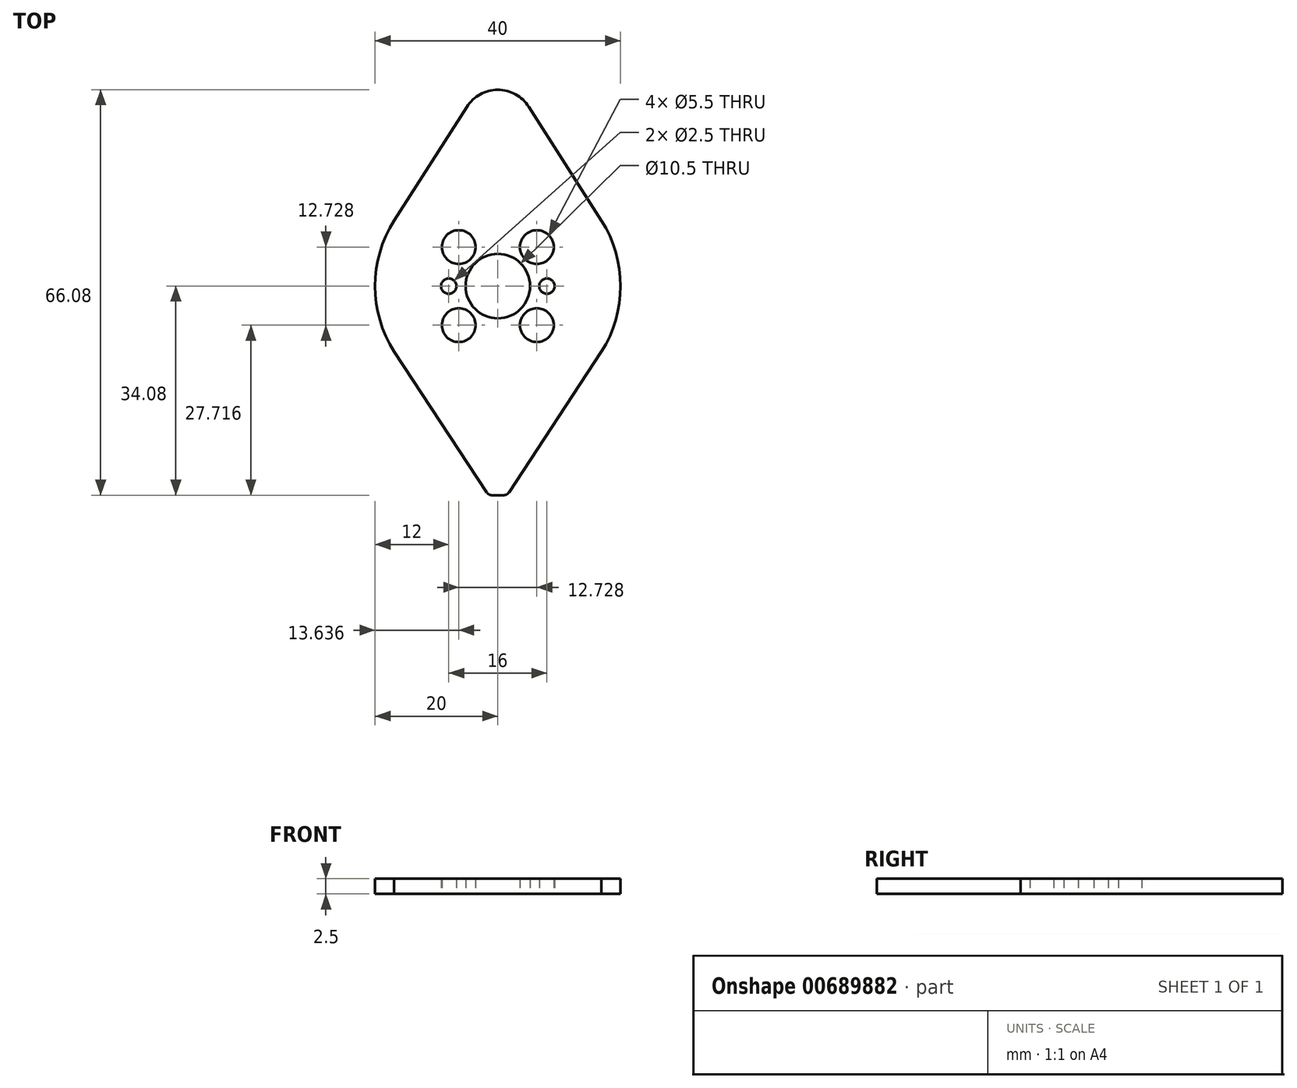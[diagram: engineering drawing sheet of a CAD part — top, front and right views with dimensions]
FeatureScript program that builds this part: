
annotation { "Feature Type Name" : "Feature", "Feature Type Description" : "" }
export const myFeature = defineFeature(function(context is Context, id is Id, definition is map)
    precondition{}
    {
        {
            var Q0;
            Q0=qCreatedBy(makeId("Top.planeOp"),FACE);
            var sketch = newSketch(context, id + "F0", { "sketchPlane" : qUnion([Q0])});
            skCircle(sketch, "E0", {"center": v(0, 0) * mm, "radius": 20 * mm});
            skCircle(sketch, "E1", {"center": v(0, 26) * mm, "radius": 6 * mm});
            skLineSegment(sketch, "E2", {"start": v(16.9, 10.7) * mm, "end": v(5.06, 29.23) * mm});
            skLineSegment(sketch, "E3", {"start": v(-5.06, 29.23) * mm, "end": v(-16.9, 10.7) * mm});
            skLineSegment(sketch, "E4", {"start": v(-16.9, -10.7) * mm, "end": v(-1.8, -33.63) * mm});
            skLineSegment(sketch, "E5", {"start": v(-0.96, -34.08) * mm, "end": v(0.96, -34.08) * mm});
            skLineSegment(sketch, "E6", {"start": v(1.8, -33.63) * mm, "end": v(16.9, -10.7) * mm});
            skCircle(sketch, "E7", {"center": v(-8, 0) * mm, "radius": 1.25 * mm});
            skCircle(sketch, "E8", {"center": v(8, 0) * mm, "radius": 1.25 * mm});
            skPoint(sketch, "E9.visualSharp", {"position": v(1.5, -34.08) * mm});
            skArc(sketch, "E9.filletArc", {"start": v(0.96, -34.08) * mm, "mid": v(1.44, -33.96) * mm, "end": v(1.8, -33.63) * mm});
            skPoint(sketch, "E10.visualSharp", {"position": v(-1.5, -34.08) * mm});
            skArc(sketch, "E10.filletArc", {"start": v(-1.8, -33.63) * mm, "mid": v(-1.44, -33.96) * mm, "end": v(-0.96, -34.08) * mm});
            skCircle(sketch, "E11", {"center": v(6.36, 6.36) * mm, "radius": 2.75 * mm});
            skCircle(sketch, "E12", {"center": v(-6.36, -6.36) * mm, "radius": 2.75 * mm});
            skCircle(sketch, "E13", {"center": v(6.36, -6.36) * mm, "radius": 2.75 * mm});
            skCircle(sketch, "E14", {"center": v(-6.36, 6.36) * mm, "radius": 2.75 * mm});
            skCircle(sketch, "E15", {"center": v(0, 0) * mm, "radius": 5.25 * mm});
            skSolve(sketch);
        }
        {
            var Q0;
            {var subQ0=sQuery(id+"F0.wireOp",EDGE,"E1");var subQ1=makeQuery(id+"F0.imprint","INTERSECT",VERTEX,{"derivedFrom":[subQ0,sQuery(id+"F0.wireOp",EDGE,"E2")]});Q0=makeQuery(id+"F0.imprint","IMPRINT",FACE,{"disambiguationData":[TD([[makeQuery(id+"F0.imprint","IMPRINT",EDGE,{"disambiguationData":[TD([[subQ1,-1.0]])],"derivedFrom":subQ0}),1.0]])]});}
            var Q1;
            {var subQ0=sQuery(id+"F0.wireOp",EDGE,"E2");Q1=makeQuery(id+"F0.imprint","IMPRINT",FACE,{"disambiguationData":[TD([[makeQuery(id+"F0.imprint","IMPRINT",EDGE,{"derivedFrom":subQ0}),1.0]])]});}
            var Q2;
            {var subQ0=sQuery(id+"F0.wireOp",EDGE,"E3");Q2=makeQuery(id+"F0.imprint","IMPRINT",FACE,{"disambiguationData":[TD([[makeQuery(id+"F0.imprint","IMPRINT",EDGE,{"derivedFrom":subQ0}),1.0]])]});}
            var Q3;
            Q3=makeQuery(id+"F0.imprint","IMPRINT",FACE,{"disambiguationData":[TD([[makeQuery(id+"F0.imprint","IMPRINT",EDGE,{"derivedFrom":sQuery(id+"F0.wireOp",EDGE,"E7")}),-1.0]])]});
            var Q4;
            Q4=makeQuery(id+"F0.imprint","IMPRINT",FACE,{"disambiguationData":[TD([[makeQuery(id+"F0.imprint","IMPRINT",EDGE,{"derivedFrom":sQuery(id+"F0.wireOp",EDGE,"E5")}),1.0]])]});
            extrude(context, id + "F1", {"entities" : qUnion([Q0, Q1, Q2, Q3, Q4]), "depth" : 2.5 * mm, "offsetDistance" : 25 * mm});
        }
    });
